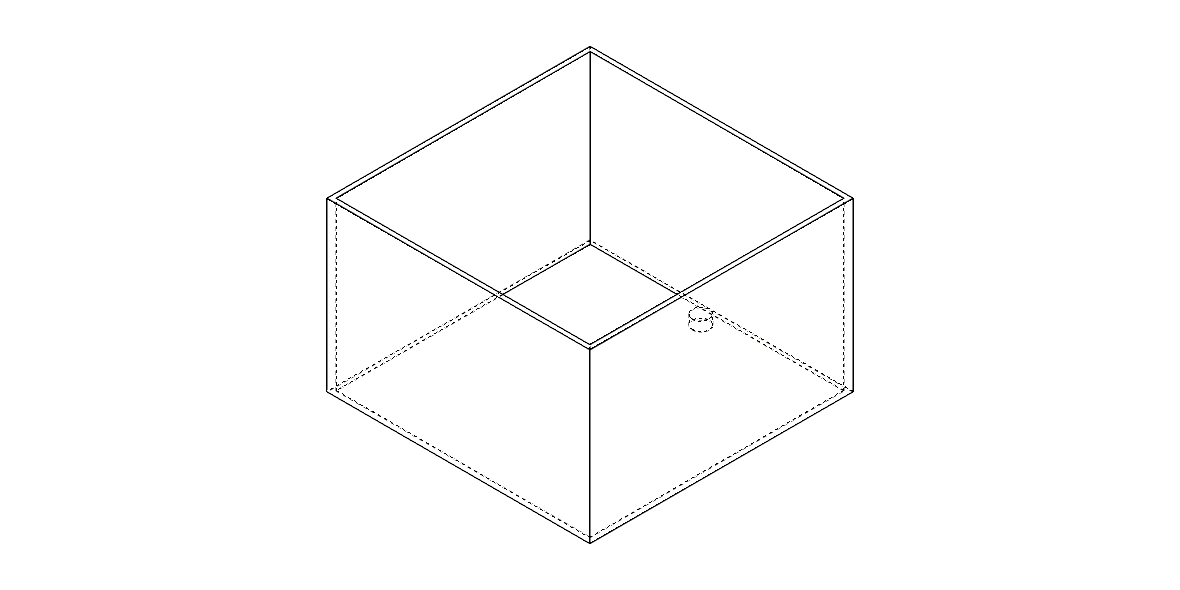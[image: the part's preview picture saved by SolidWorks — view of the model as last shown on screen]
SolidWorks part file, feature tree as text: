
SOLIDWORKS PART (.sldprt)
format: sldprt  version: not decoded by parser v0  size: 389,120 bytes
history: native  units: mm
features: sketch x4, extrude x2, material x1, cut_extrude x1 (+13 scaffold rows collapsed)
feature tree (21):
  scaffold x13  (default folders/planes/origin — collapsed)
  material  "Material <not specified>"
  sketch  "Sketch1"  dims[D1=184.15mm D2=184.15mm]
  extrude  "Boss-Extrude1"  Depth=139.7mm
  sketch  "Sketch2"  dims[D1=177.8mm D2=177.8mm]
  cut_extrude  "Cut-Extrude1"  Depth=133.35mm
  sketch  "Sketch3"  dims[c1.D2=~7.674592mm c1.D1=91.059mm c2.D2=13.462mm]
  extrude  "Boss-Extrude2"  Depth=6.604mm
  sketch  "Sketch4"
decode coverage: 6 of 7 modeling features carry decoded parameters
note: ~ marks probable driven/reference dimensions
note: suppression state not decoded; provenance and decode notes live in map.json
